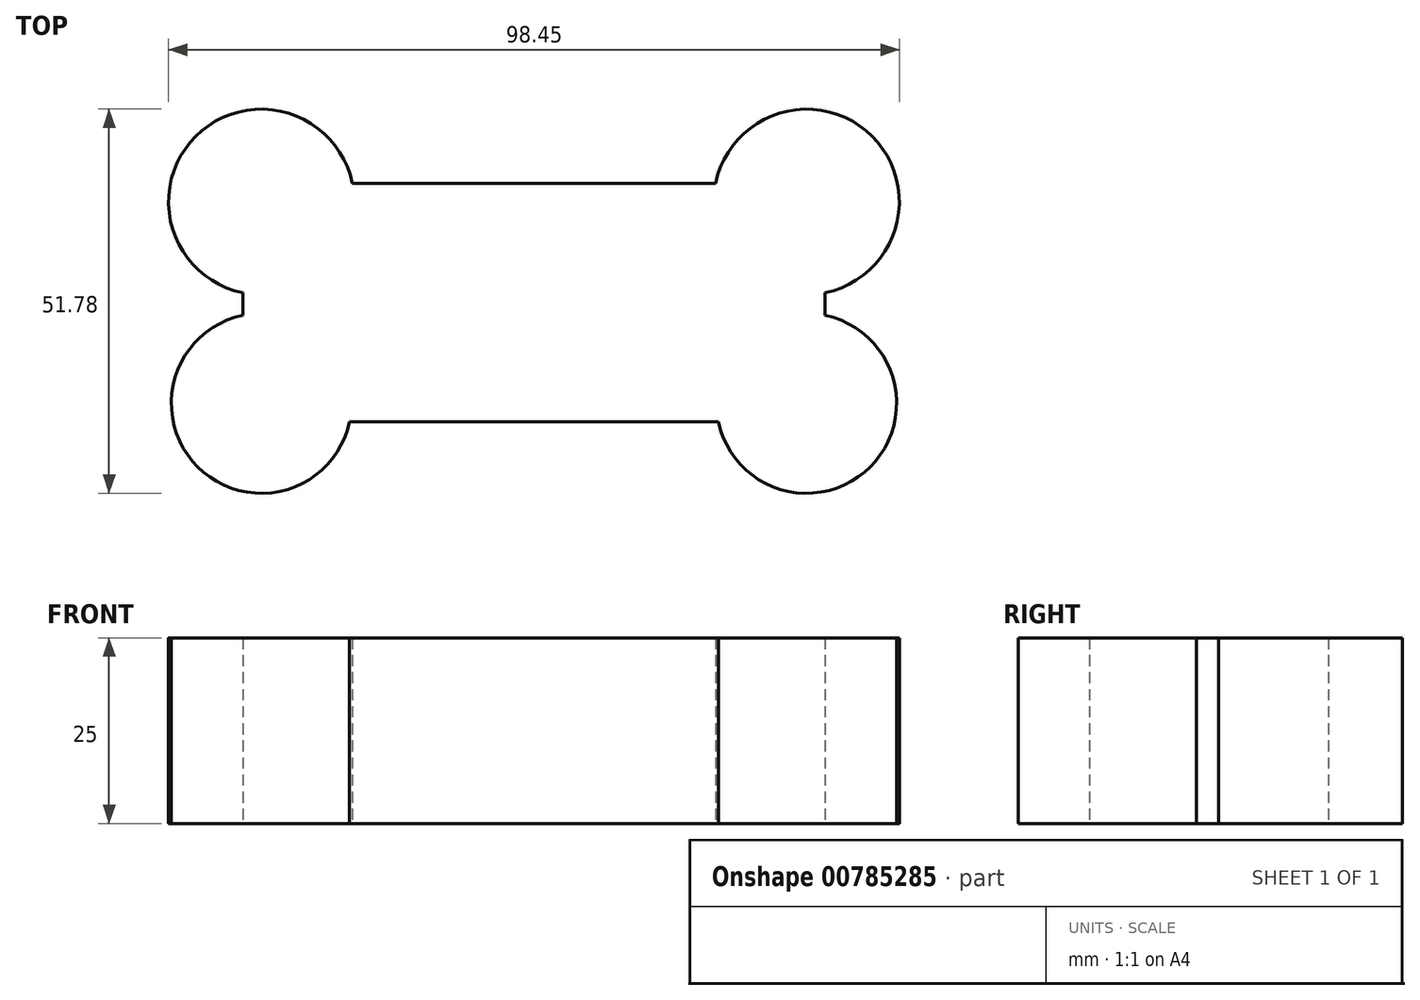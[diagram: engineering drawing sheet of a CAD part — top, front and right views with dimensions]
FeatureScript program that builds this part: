
annotation { "Feature Type Name" : "Feature", "Feature Type Description" : "" }
export const myFeature = defineFeature(function(context is Context, id is Id, definition is map)
    precondition{}
    {
        {
            var Q0;
            Q0=qCreatedBy(makeId("Top.planeOp"),FACE);
            var sketch = newSketch(context, id + "F0", { "sketchPlane" : qUnion([Q0])});
            skLineSegment(sketch, "E0.bottom", {"start": v(25.08, -16.1) * mm, "end": v(-24.63, -16.1) * mm});
            skLineSegment(sketch, "E0.top", {"start": v(24.7, 16.05) * mm, "end": v(-24.25, 16.05) * mm});
            skLineSegment(sketch, "E0.left", {"start": v(39.45, -1.73) * mm, "end": v(39.45, 1.3) * mm});
            skLineSegment(sketch, "E0.right", {"start": v(-39, -1.73) * mm, "end": v(-39, 1.3) * mm});
            skPoint(sketch, "E0.middle", {"position": v(-1.78, -0.02) * mm});
            skArc(sketch, "E1", {"start": v(39.45, 1.3) * mm, "mid": v(45.79, 22.39) * mm, "end": v(24.7, 16.05) * mm});
            skArc(sketch, "E2", {"start": v(25.08, -16.1) * mm, "mid": v(45.53, -22.18) * mm, "end": v(39.45, -1.73) * mm});
            skArc(sketch, "E3", {"start": v(-24.25, 16.05) * mm, "mid": v(-45.34, 22.39) * mm, "end": v(-39, 1.3) * mm});
            skArc(sketch, "E4", {"start": v(-39, -1.73) * mm, "mid": v(-45.08, -22.18) * mm, "end": v(-24.63, -16.1) * mm});
            skPoint(sketch, "E5.orphan", {"position": v(-39, -16.1) * mm});
            skPoint(sketch, "E6.orphan", {"position": v(-39, 16.05) * mm});
            skPoint(sketch, "E7.orphan", {"position": v(39.45, 16.05) * mm});
            skSolve(sketch);
        }
        {
            var Q0;
            Q0=makeQuery(id+"F0.imprint","IMPRINT",FACE,{"disambiguationData":[TD([[makeQuery(id+"F0.imprint","IMPRINT",EDGE,{"derivedFrom":sQuery(id+"F0.wireOp",EDGE,"E0.bottom")}),-1.0]])]});
            extrude(context, id + "F1", {"entities" : qUnion([Q0]), "depth" : 25 * mm, "offsetDistance" : 25 * mm});
        }
    });
